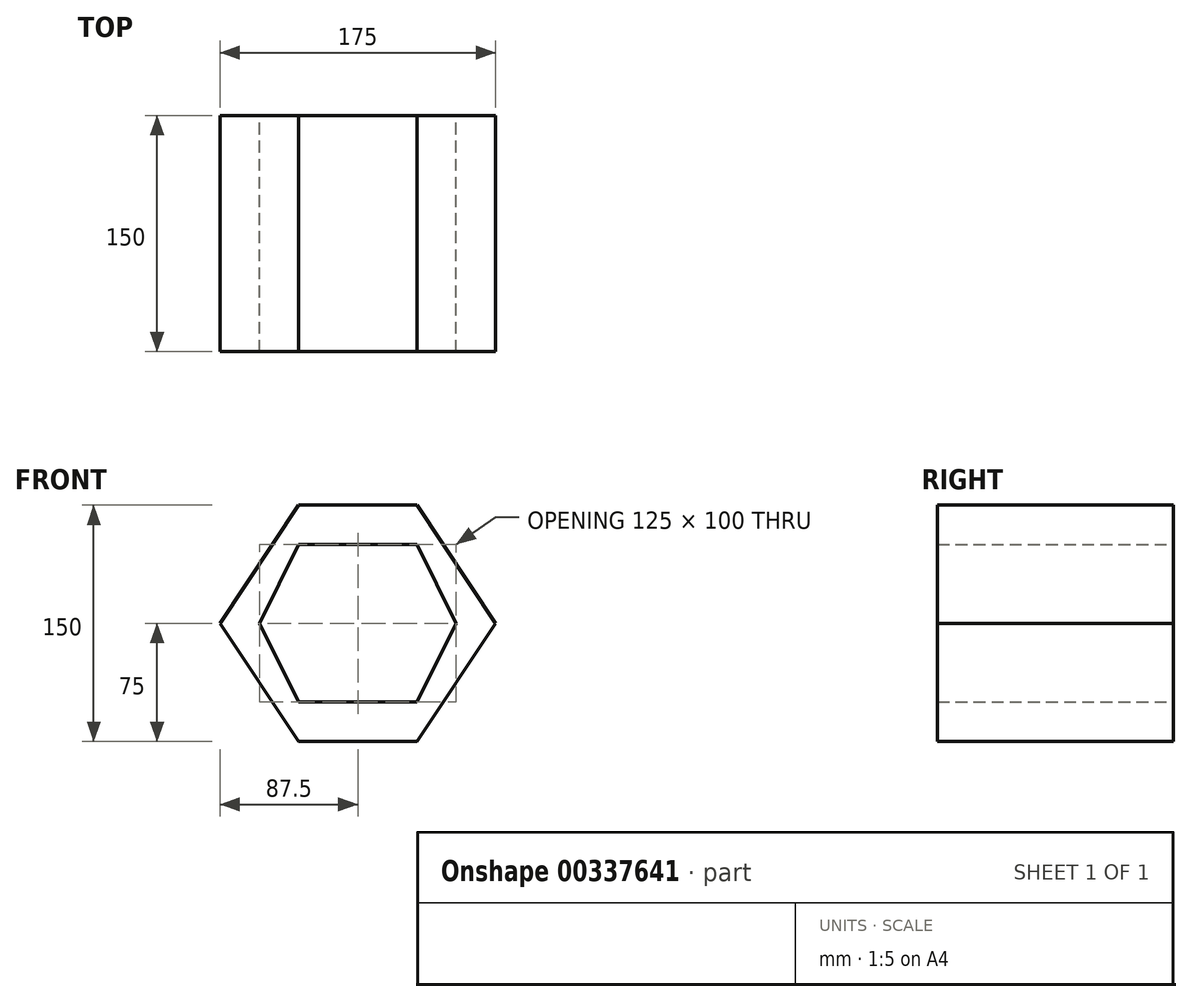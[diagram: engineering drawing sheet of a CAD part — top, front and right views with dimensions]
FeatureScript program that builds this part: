
annotation { "Feature Type Name" : "Feature", "Feature Type Description" : "" }
export const myFeature = defineFeature(function(context is Context, id is Id, definition is map)
    precondition{}
    {
        {
            var Q0;
            Q0=qCreatedBy(makeId("Front.planeOp"),FACE);
            var sketch = newSketch(context, id + "F0", { "sketchPlane" : qUnion([Q0])});
            skLineSegment(sketch, "E0.top", {"start": v(0, 75) * mm, "end": v(-75, 75) * mm});
            skLineSegment(sketch, "E0.left", {"start": v(0, 0) * mm, "end": v(0, 75) * mm});
            skLineSegment(sketch, "E0.right", {"start": v(-75, -7.5) * mm, "end": v(-75, 75) * mm});
            skLineSegment(sketch, "E1", {"start": v(-75, 75) * mm, "end": v(-125, 0) * mm});
            skLineSegment(sketch, "E2", {"start": v(-125, 0) * mm, "end": v(-75, -75) * mm});
            skLineSegment(sketch, "E3", {"start": v(-75, -75) * mm, "end": v(0, -75) * mm});
            skLineSegment(sketch, "E4", {"start": v(0, -75) * mm, "end": v(50, 0) * mm});
            skLineSegment(sketch, "E5", {"start": v(50, 0) * mm, "end": v(0, 75) * mm});
            skLineSegment(sketch, "E6", {"start": v(-75, -7.5) * mm, "end": v(-75, -75) * mm});
            skLineSegment(sketch, "E7", {"start": v(0, 0) * mm, "end": v(0, -75) * mm});
            skLineSegment(sketch, "E8", {"start": v(0, 0) * mm, "end": v(50, 0) * mm});
            skLineSegment(sketch, "E9", {"start": v(-75, 50) * mm, "end": v(0, 50) * mm});
            skLineSegment(sketch, "E10", {"start": v(0, 50) * mm, "end": v(25, 0) * mm});
            skLineSegment(sketch, "E11", {"start": v(25, 0) * mm, "end": v(0, -50) * mm});
            skLineSegment(sketch, "E12", {"start": v(0, -50) * mm, "end": v(-75, -50) * mm});
            skPoint(sketch, "E12.endSnap0", {"position": v(-75, -41.25) * mm});
            skLineSegment(sketch, "E13", {"start": v(-75, -50) * mm, "end": v(-100, 0) * mm});
            skLineSegment(sketch, "E14", {"start": v(-100, 0) * mm, "end": v(-75, 50) * mm});
            skLineSegment(sketch, "E15", {"start": v(-75, 0) * mm, "end": v(-125, 0) * mm});
            skLineSegment(sketch, "E16", {"start": v(-75, 0) * mm, "end": v(0, 0) * mm});
            skSolve(sketch);
        }
        {
            var Q0;
            Q0 = qSketchRegion(id + "F0", true);
            extrude(context, id + "F1", {"entities" : qUnion([Q0]), "depth" : 150 * mm});
        }
    });
